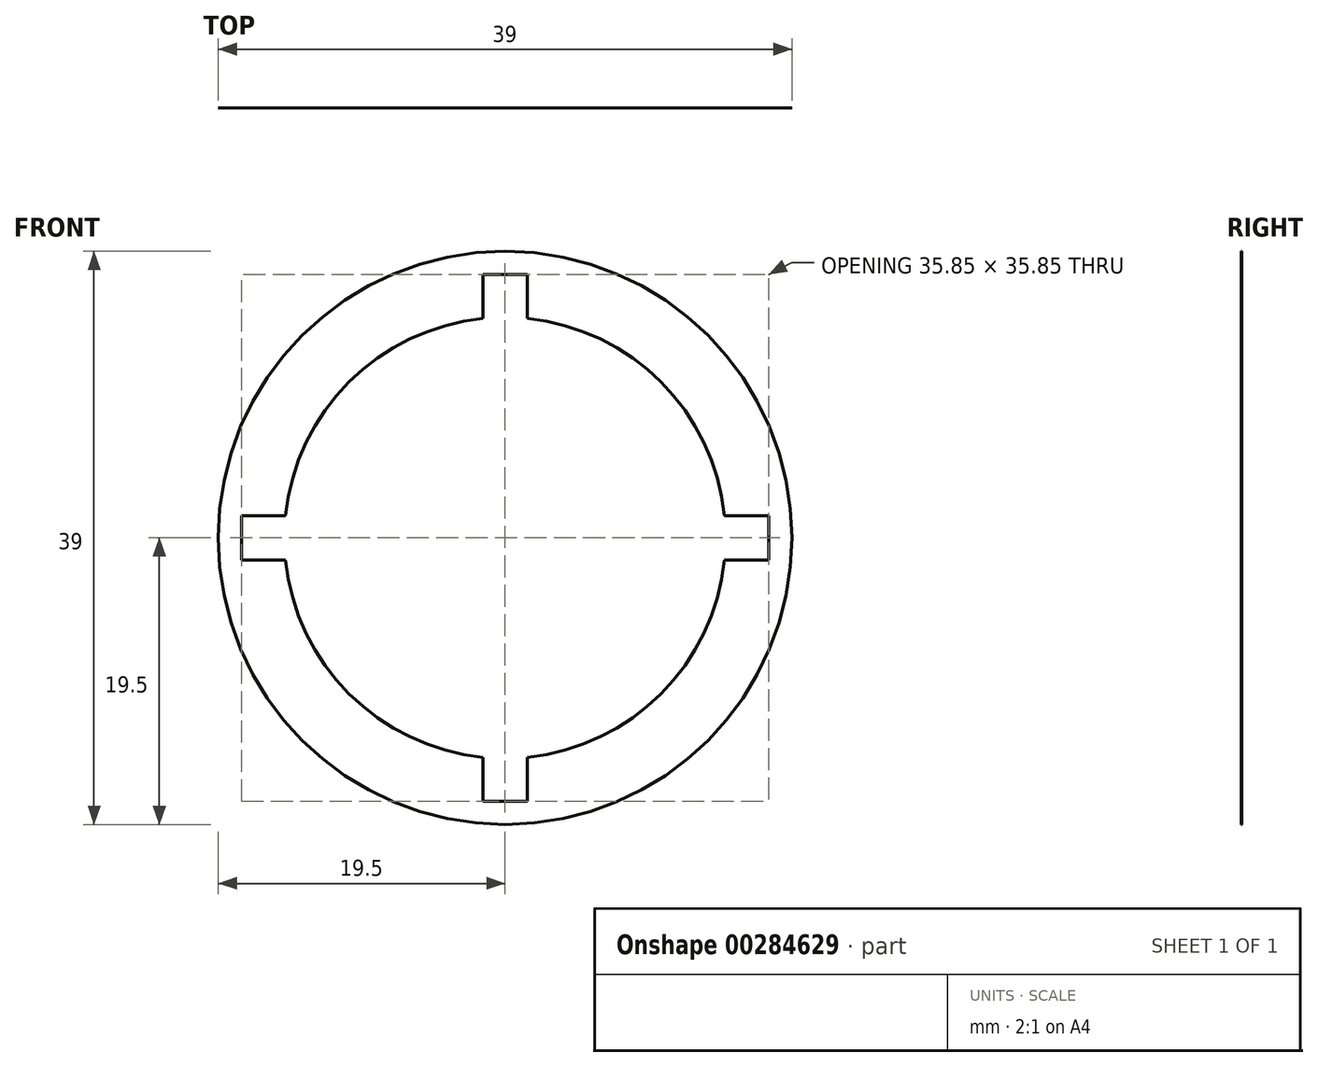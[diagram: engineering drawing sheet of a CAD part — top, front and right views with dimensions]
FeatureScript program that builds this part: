
annotation { "Feature Type Name" : "Feature", "Feature Type Description" : "" }
export const myFeature = defineFeature(function(context is Context, id is Id, definition is map)
    precondition{}
    {
        {
            var Q0;
            Q0=qCreatedBy(makeId("Front.planeOp"),FACE);
            var sketch = newSketch(context, id + "F0", { "sketchPlane" : qUnion([Q0])});
            skCircle(sketch, "E0", {"center": v(0, 0) * mm, "radius": 19.5 * mm});
            skCircle(sketch, "E1", {"center": v(0, 0) * mm, "radius": 15 * mm});
            skLineSegment(sketch, "E2", {"start": v(14.92, 1.5) * mm, "end": v(17.92, 1.5) * mm});
            skLineSegment(sketch, "E3", {"start": v(17.92, 1.5) * mm, "end": v(17.92, -1.5) * mm});
            skLineSegment(sketch, "E4", {"start": v(17.92, -1.5) * mm, "end": v(14.92, -1.5) * mm});
            skLineSegment(sketch, "E5", {"start": v(-14.92, 1.5) * mm, "end": v(-17.92, 1.5) * mm});
            skLineSegment(sketch, "E6", {"start": v(-17.92, 1.5) * mm, "end": v(-17.92, -1.5) * mm});
            skLineSegment(sketch, "E7", {"start": v(-17.92, -1.5) * mm, "end": v(-14.92, -1.5) * mm});
            skLineSegment(sketch, "E8", {"start": v(-1.5, 14.92) * mm, "end": v(-1.5, 17.92) * mm});
            skLineSegment(sketch, "E9", {"start": v(-1.5, 17.92) * mm, "end": v(1.5, 17.92) * mm});
            skLineSegment(sketch, "E10", {"start": v(1.5, 17.92) * mm, "end": v(1.5, 14.92) * mm});
            skLineSegment(sketch, "E11", {"start": v(-1.5, -14.92) * mm, "end": v(-1.5, -17.92) * mm});
            skLineSegment(sketch, "E12", {"start": v(-1.5, -17.92) * mm, "end": v(1.5, -17.92) * mm});
            skLineSegment(sketch, "E13", {"start": v(1.5, -17.92) * mm, "end": v(1.5, -14.92) * mm});
            skPoint(sketch, "E14", {"position": v(0, -17.92) * mm});
            skPoint(sketch, "E15", {"position": v(17.92, 0) * mm});
            skSolve(sketch);
        }
        {
            var Q0;
            Q0 = qSketchRegion(id + "F0", true);
            extrude(context, id + "F1", {"entities" : qUnion([Q0]), "depth" : 1 / 203.2 * mm});
        }
    });
